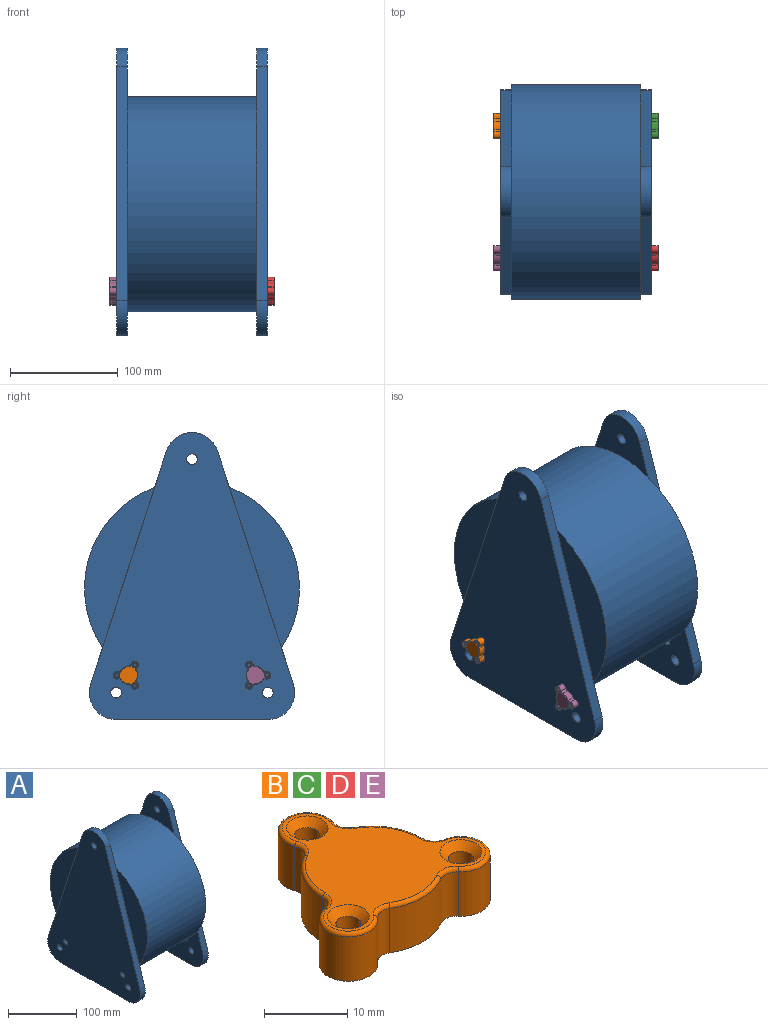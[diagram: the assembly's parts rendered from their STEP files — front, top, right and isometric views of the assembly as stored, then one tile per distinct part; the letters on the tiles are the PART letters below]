
ASSEMBLY  parts=5 mates=4
PART A: 40 faces, bbox 140x200x267.1 mm
  f0: plane 149.12x65.18mm, normal (1,0,0), area 4143.1mm2, adj f3,f16
  f1: plane 7.19x6.29mm, normal (1,0,0), area 24.9mm2, adj f3,f8
  f2: plane 7.19x6.29mm, normal (1,0,0), area 24.9mm2, adj f3,f11
  f3: cylinder r=100mm len=200mm, axis (-1,0,0), area 75398.2mm2, adj f0,f1,f2,f4,f17,f18,f19,f20
  f4: plane 149.12x65.18mm, normal (1,0,0), area 4143.1mm2, adj f3,f14
  f5: plane 267.08x191.07mm, normal (1,0,0), area 31878.4mm2, adj f6,f7,f8,f9,f10,f11,f12,f13
  f6: cylinder r=5mm len=10mm, axis (-1,0,0), area 314.2mm2, adj f5,f17
  f7: cylinder r=25mm len=32.73mm, axis (-1,0,0), area 471.2mm2, adj f5,f12,f16,f18
  f8: cylinder r=4mm len=10mm, axis (-1,0,0), area 251.3mm2, adj f1,f5,f18
  f9: cylinder r=5mm len=10mm, axis (-1,0,0), area 314.2mm2, adj f5,f18
  f10: cylinder r=5mm len=10mm, axis (-1,0,0), area 314.2mm2, adj f5,f18
  f11: cylinder r=4mm len=10mm, axis (-1,0,0), area 251.3mm2, adj f2,f5,f18
  f12: plane 141.07x10mm, normal (0,0,-1), area 1410.7mm2, adj f5,f7,f13,f18
  f13: cylinder r=25mm len=32.73mm, axis (-1,0,0), area 471.2mm2, adj f5,f12,f14,f18
  f14: plane 217.08x70.53mm, normal (0,-0.95,0.31), area 2282.5mm2, adj f4,f5,f13,f15,f17,f18
  f15: cylinder r=25mm len=47.55mm, axis (-1,0,0), area 628.3mm2, adj f5,f14,f16,f17
  f16: plane 217.08x70.53mm, normal (0,0.95,0.31), area 2282.5mm2, adj f0,f5,f7,f15,f17,f18
  f17: plane 69.64x51.26mm, normal (-1,0,0), area 2222mm2, adj f3,f6,f14,f15,f16
  f18: plane 191.07x66.71mm, normal (-1,0,0), area 6576.6mm2, adj f3,f7,f8,f9,f10,f11,f12,f13
  f19: plane 191.07x66.71mm, normal (1,0,0), area 6576.6mm2, adj f3,f21,f23,f24,f25,f26,f27,f28
  f20: plane 69.64x51.26mm, normal (1,0,0), area 2222mm2, adj f3,f21,f22,f23,f31
  f21: plane 217.08x70.53mm, normal (0,0.95,0.31), area 2282.5mm2, adj f19,f20,f22,f30,f32,f36
  f22: cylinder r=25mm len=47.55mm, axis (1,0,0), area 628.3mm2, adj f20,f21,f23,f32
  f23: plane 217.08x70.53mm, normal (0,-0.95,0.31), area 2282.5mm2, adj f19,f20,f22,f24,f32,f33
  f24: cylinder r=25mm len=32.73mm, axis (1,0,0), area 471.2mm2, adj f19,f23,f25,f32
  f25: plane 141.07x10mm, normal (0,0,-1), area 1410.7mm2, adj f19,f24,f30,f32
  f26: cylinder r=4mm len=10mm, axis (1,0,0), area 251.3mm2, adj f19,f32,f34
  f27: cylinder r=5mm len=10mm, axis (1,0,0), area 314.2mm2, adj f19,f32
  f28: cylinder r=5mm len=10mm, axis (1,0,0), area 314.2mm2, adj f19,f32
  f29: cylinder r=4mm len=10mm, axis (1,0,0), area 251.3mm2, adj f19,f32,f35
  f30: cylinder r=25mm len=32.73mm, axis (1,0,0), area 471.2mm2, adj f19,f21,f25,f32
  f31: cylinder r=5mm len=10mm, axis (1,0,0), area 314.2mm2, adj f20,f32
  f32: plane 267.08x191.07mm, normal (-1,0,0), area 31878.4mm2, adj f21,f22,f23,f24,f25,f26,f27,f28
  f33: plane 149.12x65.18mm, normal (-1,0,0), area 4143.1mm2, adj f3,f23
  f34: plane 7.19x6.29mm, normal (-1,0,0), area 24.9mm2, adj f3,f26
  f35: plane 7.19x6.29mm, normal (-1,0,0), area 24.9mm2, adj f3,f29
  f36: plane 149.12x65.18mm, normal (-1,0,0), area 4143.1mm2, adj f3,f21
  f37: plane 32x32mm, normal (1,0,0), area 804.2mm2, adj f39
  f38: plane 32x32mm, normal (-1,0,0), area 804.2mm2, adj f39
  f39: cylinder r=16mm len=120mm, axis (-1,0,0), area 12063.7mm2, adj f37,f38
PART B: 36 faces, bbox 26.6x24.1x7 mm
  f0: cylinder r=8.5mm len=7.47mm, axis (0,0,1), area 58.8mm2, adj f8,f18,f23,f33
  f1: cylinder r=8.5mm len=8.62mm, axis (0,0,1), area 58.8mm2, adj f8,f19,f20,f25
  f2: cylinder r=8.5mm len=7.47mm, axis (0,0,1), area 58.8mm2, adj f8,f21,f22,f30
  f3: cylinder r=6.5mm len=13mm, axis (0,0,1), area 204.2mm2, adj f4,f8
  f4: plane 13x13mm, normal (0,0,-1), area 19.6mm2, adj f3,f5
  f5: cylinder r=6mm len=12mm, axis (0,0,1), area 18.8mm2, adj f4,f6
  f6: plane 12x12mm, normal (0,0,-1), area 113.1mm2, adj f5
  f7: plane 25.05x22.5mm, normal (0,0,1), area 239.5mm2, adj f15,f16,f17,f24,f25,f26,f27,f28
  f8: plane 26.05x23.5mm, normal (0,0,-1), area 185.7mm2, adj f0,f1,f2,f3,f9,f10,f11,f12
  f9: cylinder r=3.5mm len=7mm, axis (0,0,-1), area 87.2mm2, adj f8,f22,f23,f34
  f10: cylinder r=1.5mm len=6mm, axis (0,0,-1), area 56.5mm2, adj f8,f17
  f11: cylinder r=3.5mm len=6.94mm, axis (0,0,-1), area 87.2mm2, adj f8,f20,f21,f26
  f12: cylinder r=1.5mm len=6mm, axis (0,0,-1), area 56.5mm2, adj f8,f16
  f13: cylinder r=3.5mm len=6.94mm, axis (0,0,-1), area 87.2mm2, adj f8,f18,f19,f29
  f14: cylinder r=1.5mm len=6mm, axis (0,0,-1), area 56.5mm2, adj f8,f15
  f15: cone r=1.5mm half-angle=45deg, axis (0,0,1), area 17.8mm2, adj f7,f14
  f16: cone r=1.5mm half-angle=45deg, axis (0,0,1), area 17.8mm2, adj f7,f12
  f17: cone r=1.5mm half-angle=45deg, axis (0,0,1), area 17.8mm2, adj f7,f10
  f18: cylinder r=2mm len=6.5mm, axis (0,0,-1), area 18.2mm2, adj f0,f8,f13,f31
  f19: cylinder r=2mm len=6.5mm, axis (0,0,1), area 18.2mm2, adj f1,f8,f13,f27
  f20: cylinder r=2mm len=6.5mm, axis (0,0,-1), area 18.2mm2, adj f1,f8,f11,f24
  f21: cylinder r=2mm len=6.5mm, axis (0,0,1), area 18.2mm2, adj f2,f8,f11,f28
  f22: cylinder r=2mm len=6.5mm, axis (0,0,-1), area 18.2mm2, adj f2,f8,f9,f32
  f23: cylinder r=2mm len=6.5mm, axis (0,0,1), area 18.2mm2, adj f0,f8,f9,f35
  f24: torus R=2.5mm, axis (0,0,-1), area 2.4mm2, adj f7,f20,f25,f26
  f25: torus R=8mm, axis (0,0,-1), area 6.9mm2, adj f1,f7,f24,f27
  f26: torus R=3mm, axis (0,0,-1), area 10mm2, adj f7,f11,f24,f28
  f27: torus R=2.5mm, axis (0,0,-1), area 2.4mm2, adj f7,f19,f25,f29
  f28: torus R=2.5mm, axis (0,0,-1), area 2.4mm2, adj f7,f21,f26,f30
  f29: torus R=3mm, axis (0,0,-1), area 10mm2, adj f7,f13,f27,f31
  f30: torus R=8mm, axis (0,0,-1), area 6.9mm2, adj f2,f7,f28,f32
  f31: torus R=2.5mm, axis (0,0,-1), area 2.4mm2, adj f7,f18,f29,f33
  f32: torus R=2.5mm, axis (0,0,-1), area 2.4mm2, adj f7,f22,f30,f34
  f33: torus R=8mm, axis (0,0,-1), area 6.9mm2, adj f0,f7,f31,f35
  f34: torus R=3mm, axis (0,0,-1), area 10mm2, adj f7,f9,f32,f35
  f35: torus R=2.5mm, axis (0,0,-1), area 2.4mm2, adj f7,f23,f33,f34
PART C: same geometry as B
PART D: same geometry as B
PART E: same geometry as B
PLACE A t=(-8.43,-0.01,-7.15)mm
PLACE B rot(axis=(0,-1,0),90deg) t=(-78.43,58.77,-88.06)mm
PLACE C rot(axis=(0,1,0),90deg) t=(61.57,58.77,-88.06)mm
PLACE D rot(axis=(0.71,0,0.71),180deg) t=(61.57,-58.79,-88.06)mm
PLACE E rot(axis=(0.71,0,-0.71),180deg) t=(-78.43,-58.79,-88.06)mm
MATE fastened E.f0 <-> A.f11  axis (1,0,0) through (-78.43,-58.79,-88.06)mm
MATE fastened D.f0 <-> A.f11  axis (-1,0,0) through (61.57,-58.79,-88.06)mm
MATE fastened B.f0 <-> A.f8  axis (1,0,0) through (-78.43,58.77,-88.06)mm
MATE fastened C.f0 <-> A.f8  axis (-1,0,0) through (61.57,58.77,-88.06)mm
